# Revit family: IS_iLifeB_T4604_BIM_NL
name_source: partatom
category: Plumbing Fixtures
units: mm (PartAtom-declared; Revit-internal decimal feet)

## family parameters
Always vertical = No
Cut with Voids When Loaded = No
OmniClass Number = 23.45.05.14.14
OmniClass Title = Sinks/Lavatories
Part Type = Normal
Room Calculation Point = No
Round Connector Dimension = Use Diameter
Shared = No
Work Plane-Based = No

## types (3) — shared parameters
Accesoires = https://www.idealstandard.nl
Accessories = https://www.idealstandard.nl
Afmetingen = 810 x 514 x 180 mm
AfstandsEenheid = Millimeter
AreaMeasurement = Internal
AreaUnits = Millimetres
AssetType = Fixed
Auteur = Ideal Standard
BIMObjectName = IS_IdealStandard_Integralwashbasinsandvanitytops_i.lifeB_T4604
BIMobject category = Wash Basins
BIMobject category code = wash-basins
BIMobject main category = Sanitary
BIMobject main category code = sanitary
Beschrijvinggarantie = Herstellergarantie
BimObjectNaam = IS_IdealStandard_Integralwashbasinsandvanitytops_i.lifeB_T4604
Brand = Ideal Standard
Brand url = https://www.idealstandard.nl
Breedte = 809.7577
Category = Sanitary
Classification = Washbasin
ConnectionType = Plumbing
CurrencyUnit = €
CurrentRevision = 1
Date of publishing = 22/07/2022
Diepte = 514 mm
DurationUnit = Years
DuurEenheid = Jahre
Edition number = 1
ElementType = Fixed
ExpectedLife = 99
Garantieonderdelen = 5
Garantieunits = Jahre
GemaaktOp = 22/07/2022
Help = https://www.idealstandard.nl
Hoogte = 180.021306570566
Hulp = https://www.idealstandard.nl
IFC Classification = Sanitary Terminal
IfcExportAs = IfcSanitaryTerminalType
IfcExportType = WASHHANDBASIN
Installatieinstructies = https://www.idealstandard.nl
Installation instructions = https://www.idealstandard.nl
InstallationInstructions = https://www.idealstandard.nl
Lengte = 514 mm
LinearUnits = millimitres
MaintenanceInformation = https://www.idealstandard.nl
Manufacturer = Ideal Standard
Manufacturer name = Ideal Standard
ManufacturerURL = https://www.idealstandard.nl
Materiaal = Schamotte
Material = Fireclay
Material main = Fireclay
Merk = Ideal Standard
ModelReference = Ideal Standard i.life B vanity 84 cm with center taphole and overflow
NBS Reference Code = 45-35-70/367
NBS Reference Description = Vanity tops with integral wash basins
Name = Integralwashbasinsandvanitytops_i.lifeB_T4604_IdealStandard
NettWeight = 20.5
Nettogewicht = 20.5
NominalDepth = 514 mm
NominalHeight = 180 mm
NominalLength = 514 mm
NominalWidth = 810 mm
OmniClass Code = 23-39 29 13 21 19
OmniClass Description = Surface Water Retention Basins
OppervlakteEenheid = Millimeter
PredefinedType = Washbasin
Product Guid = 804f6a03-133a-4577-9679-8974b5afe555
Product SKU = T4604
Product certification = https://www.idealstandard.nl
Product data url = https://bimobject.com
Product family = I.Life B
Product group = Sanitary
Product name = I.Life b vanity 84 cm with center taphole
Product url = https://www.idealstandard.nl
ProductInformation = https://www.idealstandard.nl
Productinformatie = https://www.idealstandard.nl
QR code = http://bimobject.com
Referentie = Ideal Standard i.life B vanity 84 cm with center taphole and overflow
Revisie = 1
Shape = Sculptured
Size = 810 x 514 x 180 mm
Space = Internal
SpareParts = https://www.idealstandard.nl
Technical description = https://www.idealstandard.nl
Telefoonnummer = 077 355 08 08
Toepassing = Waschbecken
Typeconnectie = Installation
Typewastafel = wandhängendes Waschbecken
UNSPSC Code = 301815
URL = https://www.idealstandard.nl
Uniclass 2015 Code = Pr_40_20_96_42
Uniclass 2015 Name = Integral washbasins and vanity tops
Uniclass2015Beschrijving = Integral washbasins and vanity tops
Uniclass2015Code = Pr_40_20_96_42
Uniclass2015Referentie = Pr_40_20_96_42
Uniclass2015Title = Integral washbasins and vanity tops
Uniclass2015Version = v1.26
Urlproducent = https://www.idealstandard.nl
ValutaEenheid = Euro
Versie = 1
Version = 1
Verwachtelevensduur = 5
VolumeUnits = Liters
Volumeunits = Liter
Vorm = Skulptur
WRASURL = https://www.wrasapprovals.co.uk
WarrantyDescription = manufacturer warranty
WarrantyDurationUnit = years
WashHandBasinMounting = Wall hung
WashHandBasinType = Vanity washbasin
Weight Net (Kg) = 51.4
Wisselstukken = https://www.idealstandard.nl
Youtube clip = https://www.youtube.com
zero-valued in all types: BrutoGewicht, Cost, Default Elevation, Vervangingskosten

## per-type parameters (varying)
| type | Afwerking | Artikelnummer | Artikelomschrijving | Artikelreferentie | BarCode | Color | Description | Eigenschappen | Features | Finish | GTIN code | Kleur | MainColor | Model | ModelNumber |
| T460401 - Ideal Standard i.life B vanity 84 cm with center taphole and overflow - White Finish | Weiss | T460401 | Ideal Standard i.life B Waschtisch 84 cm mit Hahnlochmitte, mit Überlauf, weiß, im Karton, EU-Palette | T460401 | 8014140485988 | White | Ideal Standard i.life B vanity 84 cm with center taphole, with overflow, white, in carton box, EU pallet | Waschtisch 84 cm mit Hahnlochmitte, mit Überlauf, weiß, im Karton, EU-Palette | vanity 84 cm with center taphole, with overflow, in carton box, EU pallet | White | 8014140485988 | Weiss | White | T460401 | T460401 |
| T4604MA - Ideal Standard i.life B vanity 84 cm with center taphole and overflow  - Ideal Plus White | Ideal plus Weiß | T4604MA | Ideal Standard i.life B Waschtisch 84 cm mit Hahnlochmitte, mit Überlauf, weiß Ideal Plus, im Karton, EU-Palette | T4604MA | 8014140486770 | Ideal Plus White | Ideal Standard i.life B vanity 84 cm with center taphole, with overflow, white Ideal Plus, in carton box, EU pallet | Waschtisch 84 cm mit Hahnlochmitte, mit Überlauf, weiß Ideal Plus, im Karton, EU-Palette | vanity 84 cm with center taphole, with overflow,  Ideal Plus, in carton box, EU pallet | Ideal Plus White | 8014140486770 | Ideal plus Weiß | Ideal Plus White | T4604MA | T4604MA |
| T460458 - Ideal Standard i.life B vanity 84 cm with center taphole and overflow - Glossy grey | Glänzend grau | T460458 | Ideal Standard i.life B Waschtisch 84 cm mit Hahnlochmitte, mit Überlauf, glänzend grau, im Karton, EU-Palette | T460458 | 8014140512004 | Glossy grey | Ideal Standard i.life B vanity 84 cm with center taphole, with overflow, glossy grey, in carton box, EU pallet | Waschtisch 84 cm mit Hahnlochmitte, mit Überlauf, weiß Ideal Plus, im Karton, EU-Palette | vanity 84 cm with center taphole, with overflow, in carton box, EU pallet | Glossy grey | 8014140512004 | Glänzend grau | Glossy grey | T460458 | T460458 |

## geometry (parser evidence)
native form markers: Blend x4, Sweep x4
no freeform markers — native parametric forms only
